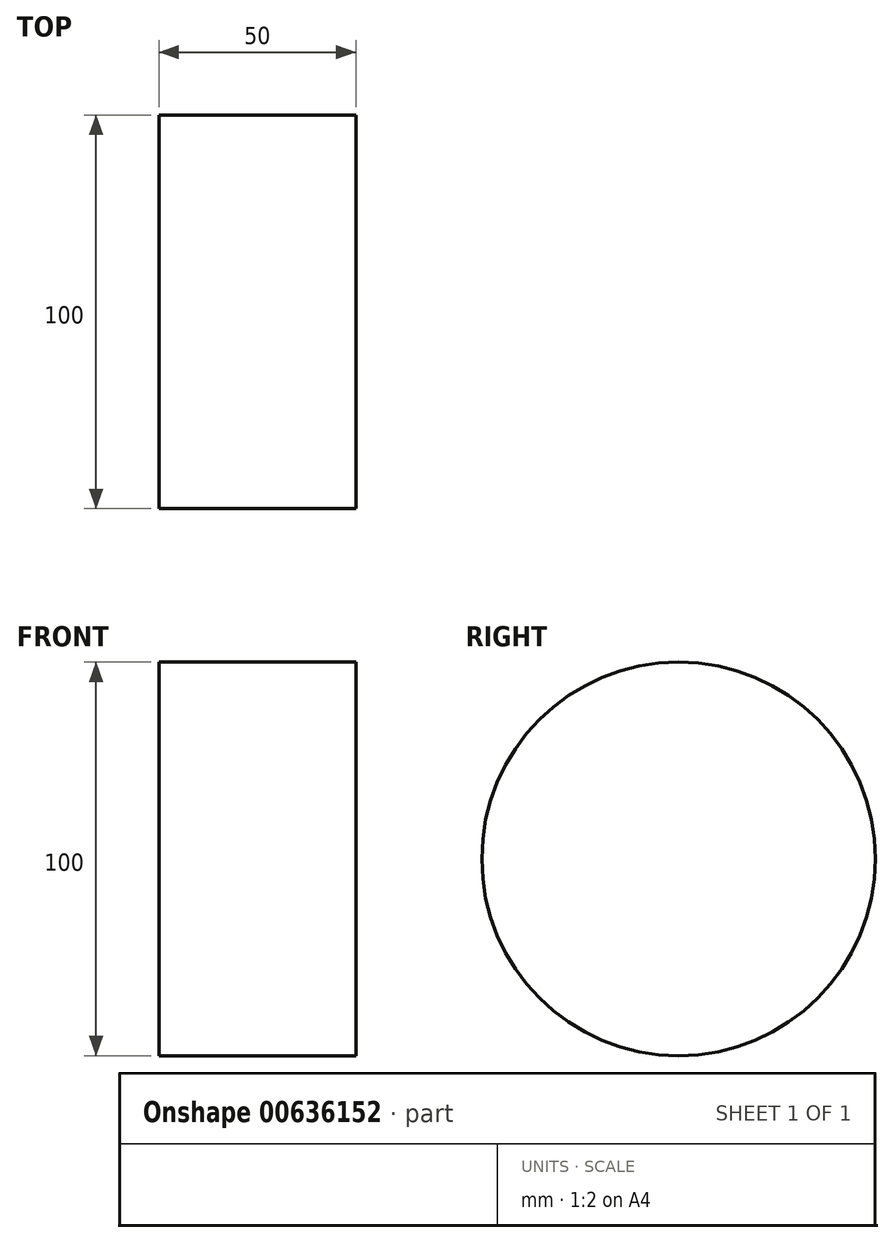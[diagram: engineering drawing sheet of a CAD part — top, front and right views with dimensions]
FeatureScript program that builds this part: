
annotation { "Feature Type Name" : "Feature", "Feature Type Description" : "" }
export const myFeature = defineFeature(function(context is Context, id is Id, definition is map)
    precondition{}
    {
        {
            var Q0;
            Q0=qCreatedBy(makeId("Front.planeOp"),FACE);
            var sketch = newSketch(context, id + "F0", { "sketchPlane" : qUnion([Q0])});
            skLineSegment(sketch, "E0", {"start": v(-50.78, 0) * mm, "end": v(57.4, 0) * mm});
            skLineSegment(sketch, "E1", {"start": v(-31.16, 0) * mm, "end": v(-31.16, 50) * mm});
            skLineSegment(sketch, "E2", {"start": v(18.84, 50) * mm, "end": v(18.84, 0) * mm});
            skLineSegment(sketch, "E3", {"start": v(-31.16, 50) * mm, "end": v(18.84, 50) * mm});
            skSolve(sketch);
        }
        {
            var Q0;
            {var subQ0=sQuery(id+"F0.wireOp",EDGE,"E1");Q0=makeQuery(id+"F0.imprint","IMPRINT",FACE,{"disambiguationData":[TD([[makeQuery(id+"F0.imprint","IMPRINT",EDGE,{"derivedFrom":subQ0}),-1.0]])]});}
            var Q1;
            Q1=sQuery(id+"F0.wireOp",EDGE,"E0");
            revolve(context, id + "F1", {"entities" : qUnion([Q0]), "axis" : qUnion([Q1]), "revolveType" : RevolveType.FULL});
        }
    });
